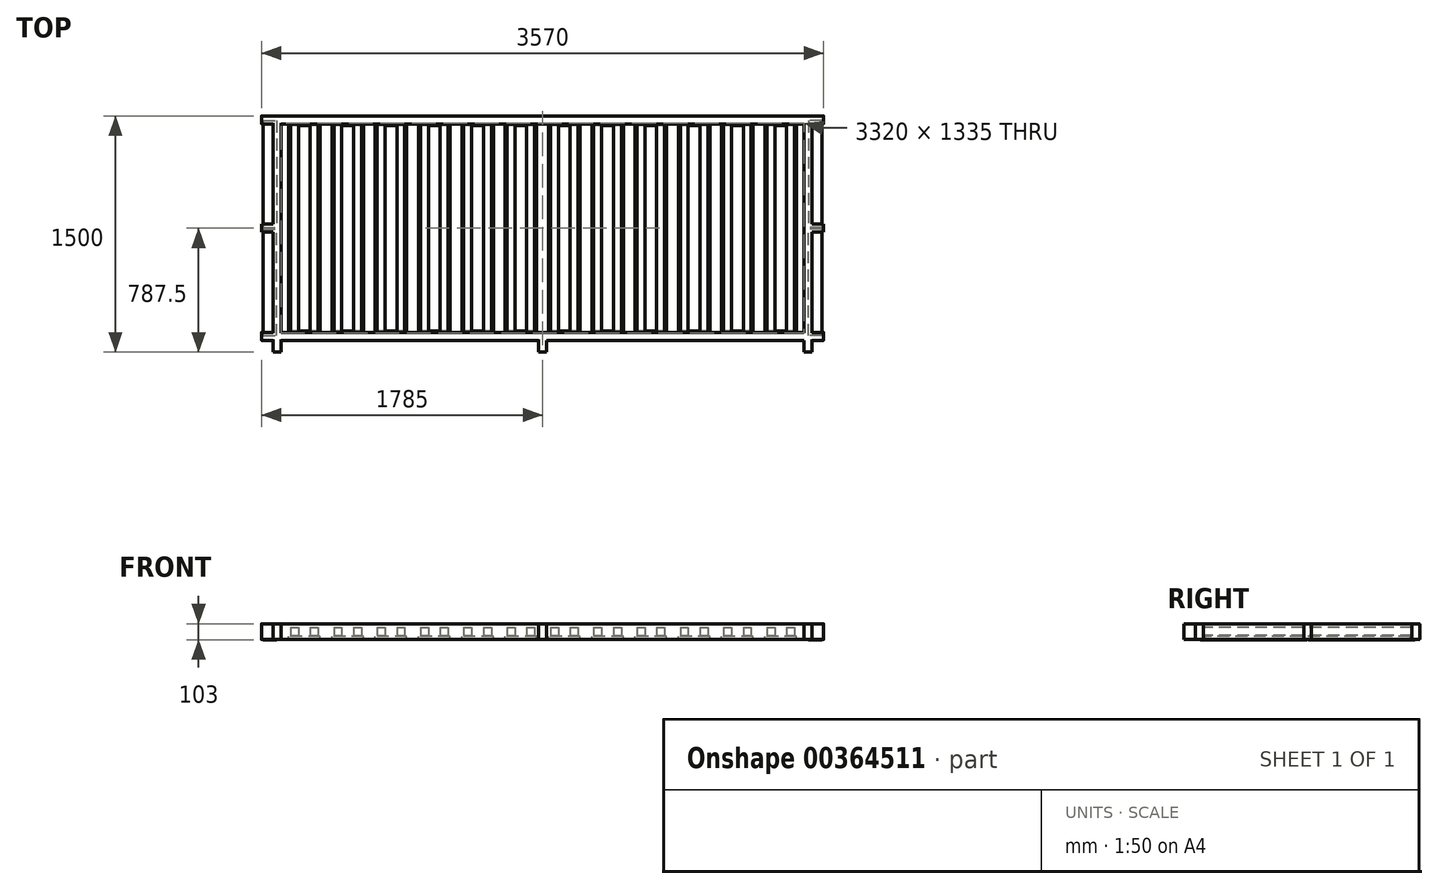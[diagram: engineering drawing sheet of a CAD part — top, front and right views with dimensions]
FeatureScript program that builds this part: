
annotation { "Feature Type Name" : "Feature", "Feature Type Description" : "" }
export const myFeature = defineFeature(function(context is Context, id is Id, definition is map)
    precondition{}
    {
        {
            var Q0;
            Q0=qCreatedBy(makeId("Top.planeOp"),FACE);
            var sketch = newSketch(context, id + "F0", { "sketchPlane" : qUnion([Q0])});
            skLineSegment(sketch, "E0.bottom", {"start": v(0, 0) * mm, "end": v(3570, 0) * mm, "construction": true});
            skLineSegment(sketch, "E0.top", {"start": v(0, 1500) * mm, "end": v(3570, 1500) * mm, "construction": true});
            skLineSegment(sketch, "E0.left", {"start": v(0, 0) * mm, "end": v(0, 1500) * mm, "construction": true});
            skLineSegment(sketch, "E0.right", {"start": v(3570, 0) * mm, "end": v(3570, 1500) * mm, "construction": true});
            skLineSegment(sketch, "E1.bottom", {"start": v(0, 1500) * mm, "end": v(3570, 1500) * mm});
            skLineSegment(sketch, "E1.top", {"start": v(0, 1450) * mm, "end": v(3570, 1450) * mm});
            skLineSegment(sketch, "E1.left", {"start": v(0, 1500) * mm, "end": v(0, 1450) * mm});
            skLineSegment(sketch, "E1.right", {"start": v(3570, 1500) * mm, "end": v(3570, 1450) * mm});
            skLineSegment(sketch, "E2.bottom", {"start": v(0, 125) * mm, "end": v(3570, 125) * mm});
            skLineSegment(sketch, "E2.top", {"start": v(0, 75) * mm, "end": v(3570, 75) * mm});
            skLineSegment(sketch, "E2.left", {"start": v(0, 125) * mm, "end": v(0, 75) * mm});
            skLineSegment(sketch, "E2.right", {"start": v(3570, 125) * mm, "end": v(3570, 75) * mm});
            skLineSegment(sketch, "E3.bottom", {"start": v(75, 1500) * mm, "end": v(125, 1500) * mm});
            skLineSegment(sketch, "E3.top", {"start": v(75, 0) * mm, "end": v(125, 0) * mm});
            skLineSegment(sketch, "E3.left", {"start": v(75, 1500) * mm, "end": v(75, 0) * mm});
            skLineSegment(sketch, "E3.right", {"start": v(125, 1500) * mm, "end": v(125, 0) * mm});
            skLineSegment(sketch, "E4.bottom", {"start": v(3445, 1500) * mm, "end": v(3495, 1500) * mm});
            skLineSegment(sketch, "E4.top", {"start": v(3445, 0) * mm, "end": v(3495, 0) * mm});
            skLineSegment(sketch, "E4.left", {"start": v(3445, 1500) * mm, "end": v(3445, 0) * mm});
            skLineSegment(sketch, "E4.right", {"start": v(3495, 1500) * mm, "end": v(3495, 0) * mm});
            skLineSegment(sketch, "E5.bottom", {"start": v(1810, 0) * mm, "end": v(1760, 0) * mm});
            skLineSegment(sketch, "E5.left", {"start": v(1810, 0) * mm, "end": v(1810, 75) * mm});
            skLineSegment(sketch, "E5.right", {"start": v(1760, 0) * mm, "end": v(1760, 75) * mm});
            skLineSegment(sketch, "E6", {"start": v(3495, 1450) * mm, "end": v(3495, 125) * mm, "construction": true});
            skLineSegment(sketch, "E7.bottom", {"start": v(3570, 812.5) * mm, "end": v(3495, 812.5) * mm});
            skLineSegment(sketch, "E7.top", {"start": v(3570, 762.5) * mm, "end": v(3495, 762.5) * mm});
            skLineSegment(sketch, "E7.left", {"start": v(3570, 812.5) * mm, "end": v(3570, 762.5) * mm});
            skLineSegment(sketch, "E8", {"start": v(75, 1450) * mm, "end": v(75, 125) * mm, "construction": true});
            skLineSegment(sketch, "E9.bottom", {"start": v(0, 812.5) * mm, "end": v(75, 812.5) * mm});
            skLineSegment(sketch, "E9.top", {"start": v(0, 762.5) * mm, "end": v(75, 762.5) * mm});
            skLineSegment(sketch, "E9.left", {"start": v(0, 812.5) * mm, "end": v(0, 762.5) * mm});
            skSolve(sketch);
        }
        {
            var Q0;
            Q0 = qSketchRegion(id + "F0", true);
            extrude(context, id + "F1", {"entities" : qUnion([Q0]), "depth" : 75 * mm, "hasSecondDirection" : true, "secondDirectionOppositeDirection" : true, "secondDirectionDepth" : 25 * mm});
        }
        {
            var Q0;
            {var subQ0=sQuery(id+"F0.wireOp",EDGE,"E1.top");Q0=makeQuery(id+"F1.opExtrude","CAP_EDGE",EDGE,{"disambiguationData":[OSD([subQ0]),TDD([makeQuery(id+"F0.imprint","IMPRINT",EDGE,{"disambiguationData":[TD([[makeQuery(id+"F0.imprint","INTERSECT",VERTEX,{"derivedFrom":[subQ0,sQuery(id+"F0.wireOp",EDGE,"E3.right")]}),-1.0]])],"derivedFrom":subQ0})])],"isStart":false});}
            var Q1;
            Q1=makeQuery(id+"F1.opExtrude","CAP_EDGE",EDGE,{"disambiguationData":[OSD([sQuery(id+"F0.wireOp",EDGE,"E1.bottom"),sQuery(id+"F0.wireOp",EDGE,"E3.bottom"),sQuery(id+"F0.wireOp",EDGE,"E4.bottom")])],"isStart":false});
            var Q2;
            {var subQ0=sQuery(id+"F0.wireOp",EDGE,"E2.bottom");Q2=makeQuery(id+"F1.opExtrude","CAP_EDGE",EDGE,{"disambiguationData":[OSD([subQ0]),TDD([makeQuery(id+"F0.imprint","IMPRINT",EDGE,{"disambiguationData":[TD([[makeQuery(id+"F0.imprint","INTERSECT",VERTEX,{"derivedFrom":[subQ0,sQuery(id+"F0.wireOp",EDGE,"E3.right")]}),-1.0]])],"derivedFrom":subQ0})])],"isStart":false});}
            var Q3;
            {var subQ0=sQuery(id+"F0.wireOp",EDGE,"E2.top");Q3=makeQuery(id+"F1.opExtrude","CAP_EDGE",EDGE,{"disambiguationData":[OSD([subQ0]),TDD([makeQuery(id+"F0.imprint","IMPRINT",EDGE,{"disambiguationData":[TD([[makeQuery(id+"F0.imprint","INTERSECT",VERTEX,{"derivedFrom":[subQ0,sQuery(id+"F0.wireOp",EDGE,"E3.right")]}),-1.0]])],"derivedFrom":subQ0})])],"isStart":false});}
            var Q4;
            {var subQ0=sQuery(id+"F0.wireOp",EDGE,"E2.top");Q4=makeQuery(id+"F1.opExtrude","CAP_EDGE",EDGE,{"disambiguationData":[OSD([subQ0]),TDD([makeQuery(id+"F0.imprint","IMPRINT",EDGE,{"disambiguationData":[TD([[makeQuery(id+"F0.imprint","INTERSECT",VERTEX,{"derivedFrom":[subQ0,sQuery(id+"F0.wireOp",EDGE,"E2.left")]}),-1.0]])],"derivedFrom":subQ0})])],"isStart":false});}
            var Q5;
            {var subQ0=sQuery(id+"F0.wireOp",EDGE,"E2.bottom");Q5=makeQuery(id+"F1.opExtrude","CAP_EDGE",EDGE,{"disambiguationData":[OSD([subQ0]),TDD([makeQuery(id+"F0.imprint","IMPRINT",EDGE,{"disambiguationData":[TD([[makeQuery(id+"F0.imprint","INTERSECT",VERTEX,{"derivedFrom":[subQ0,sQuery(id+"F0.wireOp",EDGE,"E2.left")]}),-1.0]])],"derivedFrom":subQ0})])],"isStart":false});}
            var Q6;
            {var subQ0=sQuery(id+"F0.wireOp",EDGE,"E2.bottom");Q6=makeQuery(id+"F1.opExtrude","CAP_EDGE",EDGE,{"disambiguationData":[OSD([subQ0]),TDD([makeQuery(id+"F0.imprint","IMPRINT",EDGE,{"disambiguationData":[TD([[makeQuery(id+"F0.imprint","INTERSECT",VERTEX,{"derivedFrom":[subQ0,sQuery(id+"F0.wireOp",EDGE,"E2.right")]}),1.0]])],"derivedFrom":subQ0})])],"isStart":false});}
            var Q7;
            {var subQ0=sQuery(id+"F0.wireOp",EDGE,"E2.top");Q7=makeQuery(id+"F1.opExtrude","CAP_EDGE",EDGE,{"disambiguationData":[OSD([subQ0]),TDD([makeQuery(id+"F0.imprint","IMPRINT",EDGE,{"disambiguationData":[TD([[makeQuery(id+"F0.imprint","INTERSECT",VERTEX,{"derivedFrom":[subQ0,sQuery(id+"F0.wireOp",EDGE,"E2.right")]}),1.0]])],"derivedFrom":subQ0})])],"isStart":false});}
            var Q8;
            {var subQ0=sQuery(id+"F0.wireOp",EDGE,"E1.top");Q8=makeQuery(id+"F1.opExtrude","CAP_EDGE",EDGE,{"disambiguationData":[OSD([subQ0]),TDD([makeQuery(id+"F0.imprint","IMPRINT",EDGE,{"disambiguationData":[TD([[makeQuery(id+"F0.imprint","INTERSECT",VERTEX,{"derivedFrom":[subQ0,sQuery(id+"F0.wireOp",EDGE,"E1.right")]}),1.0]])],"derivedFrom":subQ0})])],"isStart":false});}
            var Q9;
            {var subQ0=sQuery(id+"F0.wireOp",EDGE,"E1.top");Q9=makeQuery(id+"F1.opExtrude","CAP_EDGE",EDGE,{"disambiguationData":[OSD([subQ0]),TDD([makeQuery(id+"F0.imprint","IMPRINT",EDGE,{"disambiguationData":[TD([[makeQuery(id+"F0.imprint","INTERSECT",VERTEX,{"derivedFrom":[subQ0,sQuery(id+"F0.wireOp",EDGE,"E1.left")]}),-1.0]])],"derivedFrom":subQ0})])],"isStart":false});}
            var Q10;
            Q10=makeQuery(id+"F1.opExtrude","CAP_EDGE",EDGE,{"disambiguationData":[OSD([sQuery(id+"F0.wireOp",EDGE,"E1.bottom"),sQuery(id+"F0.wireOp",EDGE,"E3.bottom"),sQuery(id+"F0.wireOp",EDGE,"E4.bottom")])],"isStart":true});
            var Q11;
            {var subQ0=sQuery(id+"F0.wireOp",EDGE,"E1.top");Q11=makeQuery(id+"F1.opExtrude","CAP_EDGE",EDGE,{"disambiguationData":[OSD([subQ0]),TDD([makeQuery(id+"F0.imprint","IMPRINT",EDGE,{"disambiguationData":[TD([[makeQuery(id+"F0.imprint","INTERSECT",VERTEX,{"derivedFrom":[subQ0,sQuery(id+"F0.wireOp",EDGE,"E3.right")]}),-1.0]])],"derivedFrom":subQ0})])],"isStart":true});}
            var Q12;
            {var subQ0=sQuery(id+"F0.wireOp",EDGE,"E1.top");Q12=makeQuery(id+"F1.opExtrude","CAP_EDGE",EDGE,{"disambiguationData":[OSD([subQ0]),TDD([makeQuery(id+"F0.imprint","IMPRINT",EDGE,{"disambiguationData":[TD([[makeQuery(id+"F0.imprint","INTERSECT",VERTEX,{"derivedFrom":[subQ0,sQuery(id+"F0.wireOp",EDGE,"E1.right")]}),1.0]])],"derivedFrom":subQ0})])],"isStart":true});}
            var Q13;
            {var subQ0=sQuery(id+"F0.wireOp",EDGE,"E2.top");Q13=makeQuery(id+"F1.opExtrude","CAP_EDGE",EDGE,{"disambiguationData":[OSD([subQ0]),TDD([makeQuery(id+"F0.imprint","IMPRINT",EDGE,{"disambiguationData":[TD([[makeQuery(id+"F0.imprint","INTERSECT",VERTEX,{"derivedFrom":[subQ0,sQuery(id+"F0.wireOp",EDGE,"E2.right")]}),1.0]])],"derivedFrom":subQ0})])],"isStart":true});}
            var Q14;
            {var subQ0=sQuery(id+"F0.wireOp",EDGE,"E2.bottom");Q14=makeQuery(id+"F1.opExtrude","CAP_EDGE",EDGE,{"disambiguationData":[OSD([subQ0]),TDD([makeQuery(id+"F0.imprint","IMPRINT",EDGE,{"disambiguationData":[TD([[makeQuery(id+"F0.imprint","INTERSECT",VERTEX,{"derivedFrom":[subQ0,sQuery(id+"F0.wireOp",EDGE,"E2.right")]}),1.0]])],"derivedFrom":subQ0})])],"isStart":true});}
            var Q15;
            {var subQ0=sQuery(id+"F0.wireOp",EDGE,"E2.bottom");Q15=makeQuery(id+"F1.opExtrude","CAP_EDGE",EDGE,{"disambiguationData":[OSD([subQ0]),TDD([makeQuery(id+"F0.imprint","IMPRINT",EDGE,{"disambiguationData":[TD([[makeQuery(id+"F0.imprint","INTERSECT",VERTEX,{"derivedFrom":[subQ0,sQuery(id+"F0.wireOp",EDGE,"E3.right")]}),-1.0]])],"derivedFrom":subQ0})])],"isStart":true});}
            var Q16;
            {var subQ0=sQuery(id+"F0.wireOp",EDGE,"E2.top");Q16=makeQuery(id+"F1.opExtrude","CAP_EDGE",EDGE,{"disambiguationData":[OSD([subQ0]),TDD([makeQuery(id+"F0.imprint","IMPRINT",EDGE,{"disambiguationData":[TD([[makeQuery(id+"F0.imprint","INTERSECT",VERTEX,{"derivedFrom":[subQ0,sQuery(id+"F0.wireOp",EDGE,"E3.right")]}),-1.0]])],"derivedFrom":subQ0})])],"isStart":true});}
            var Q17;
            {var subQ0=sQuery(id+"F0.wireOp",EDGE,"E2.bottom");Q17=makeQuery(id+"F1.opExtrude","CAP_EDGE",EDGE,{"disambiguationData":[OSD([subQ0]),TDD([makeQuery(id+"F0.imprint","IMPRINT",EDGE,{"disambiguationData":[TD([[makeQuery(id+"F0.imprint","INTERSECT",VERTEX,{"derivedFrom":[subQ0,sQuery(id+"F0.wireOp",EDGE,"E2.left")]}),-1.0]])],"derivedFrom":subQ0})])],"isStart":true});}
            var Q18;
            {var subQ0=sQuery(id+"F0.wireOp",EDGE,"E2.top");Q18=makeQuery(id+"F1.opExtrude","CAP_EDGE",EDGE,{"disambiguationData":[OSD([subQ0]),TDD([makeQuery(id+"F0.imprint","IMPRINT",EDGE,{"disambiguationData":[TD([[makeQuery(id+"F0.imprint","INTERSECT",VERTEX,{"derivedFrom":[subQ0,sQuery(id+"F0.wireOp",EDGE,"E2.left")]}),-1.0]])],"derivedFrom":subQ0})])],"isStart":true});}
            var Q19;
            {var subQ0=sQuery(id+"F0.wireOp",EDGE,"E1.top");Q19=makeQuery(id+"F1.opExtrude","CAP_EDGE",EDGE,{"disambiguationData":[OSD([subQ0]),TDD([makeQuery(id+"F0.imprint","IMPRINT",EDGE,{"disambiguationData":[TD([[makeQuery(id+"F0.imprint","INTERSECT",VERTEX,{"derivedFrom":[subQ0,sQuery(id+"F0.wireOp",EDGE,"E1.left")]}),-1.0]])],"derivedFrom":subQ0})])],"isStart":true});}
            fillet(context, id + "F2", {"entities" : qUnion([Q0, Q1, Q2, Q3, Q4, Q5, Q6, Q7, Q8, Q9, Q10, Q11, Q12, Q13, Q14, Q15, Q16, Q17, Q18, Q19]), "radius" : 5 * mm, "tangentPropagation" : true, "allowEdgeOverflow" : false});
        }
        {
            var Q0;
            Q0=qCreatedBy(makeId("Top.planeOp"),FACE);
            var sketch = newSketch(context, id + "F3", { "sketchPlane" : qUnion([Q0])});
            skLineSegment(sketch, "E10.bottom", {"start": v(185, 1450) * mm, "end": v(235, 1450) * mm});
            skLineSegment(sketch, "E10.top", {"start": v(185, 125) * mm, "end": v(235, 125) * mm});
            skLineSegment(sketch, "E10.left", {"start": v(185, 1450) * mm, "end": v(185, 125) * mm});
            skLineSegment(sketch, "E10.right", {"start": v(235, 1450) * mm, "end": v(235, 125) * mm});
            skLineSegment(sketch, "E11.bottom", {"start": v(310, 1450) * mm, "end": v(360, 1450) * mm});
            skLineSegment(sketch, "E11.top", {"start": v(310, 125) * mm, "end": v(360, 125) * mm});
            skLineSegment(sketch, "E11.left", {"start": v(310, 1450) * mm, "end": v(310, 125) * mm});
            skLineSegment(sketch, "E11.right", {"start": v(360, 1450) * mm, "end": v(360, 125) * mm});
            skLineSegment(sketch, "E12", {"start": v(235, 125) * mm, "end": v(387, 125) * mm, "construction": true});
            skLineSegment(sketch, "E13", {"start": v(235, 1450) * mm, "end": v(386.34, 1450) * mm, "construction": true});
            skLineSegment(sketch, "E14.1.0.0", {"start": v(635, 1450) * mm, "end": v(635, 125) * mm});
            skLineSegment(sketch, "E14.1.0.1", {"start": v(585, 1450) * mm, "end": v(585, 125) * mm});
            skLineSegment(sketch, "E14.1.0.2", {"start": v(510, 1450) * mm, "end": v(510, 125) * mm});
            skLineSegment(sketch, "E14.1.0.3", {"start": v(460, 1450) * mm, "end": v(460, 125) * mm});
            skLineSegment(sketch, "E14.1.0.4", {"start": v(460, 125) * mm, "end": v(510, 125) * mm});
            skLineSegment(sketch, "E14.1.0.5", {"start": v(460, 1450) * mm, "end": v(510, 1450) * mm});
            skLineSegment(sketch, "E14.1.0.6", {"start": v(585, 125) * mm, "end": v(635, 125) * mm});
            skLineSegment(sketch, "E14.1.0.7", {"start": v(585, 1450) * mm, "end": v(635, 1450) * mm});
            skLineSegment(sketch, "E14.2.0.0", {"start": v(910, 1450) * mm, "end": v(910, 125) * mm});
            skLineSegment(sketch, "E14.2.0.1", {"start": v(860, 1450) * mm, "end": v(860, 125) * mm});
            skLineSegment(sketch, "E14.2.0.2", {"start": v(785, 1450) * mm, "end": v(785, 125) * mm});
            skLineSegment(sketch, "E14.2.0.3", {"start": v(735, 1450) * mm, "end": v(735, 125) * mm});
            skLineSegment(sketch, "E14.2.0.4", {"start": v(735, 125) * mm, "end": v(785, 125) * mm});
            skLineSegment(sketch, "E14.2.0.5", {"start": v(735, 1450) * mm, "end": v(785, 1450) * mm});
            skLineSegment(sketch, "E14.2.0.6", {"start": v(860, 125) * mm, "end": v(910, 125) * mm});
            skLineSegment(sketch, "E14.2.0.7", {"start": v(860, 1450) * mm, "end": v(910, 1450) * mm});
            skLineSegment(sketch, "E14.3.0.0", {"start": v(1185, 1450) * mm, "end": v(1185, 125) * mm});
            skLineSegment(sketch, "E14.3.0.1", {"start": v(1135, 1450) * mm, "end": v(1135, 125) * mm});
            skLineSegment(sketch, "E14.3.0.2", {"start": v(1060, 1450) * mm, "end": v(1060, 125) * mm});
            skLineSegment(sketch, "E14.3.0.3", {"start": v(1010, 1450) * mm, "end": v(1010, 125) * mm});
            skLineSegment(sketch, "E14.3.0.4", {"start": v(1010, 125) * mm, "end": v(1060, 125) * mm});
            skLineSegment(sketch, "E14.3.0.5", {"start": v(1010, 1450) * mm, "end": v(1060, 1450) * mm});
            skLineSegment(sketch, "E14.3.0.6", {"start": v(1135, 125) * mm, "end": v(1185, 125) * mm});
            skLineSegment(sketch, "E14.3.0.7", {"start": v(1135, 1450) * mm, "end": v(1185, 1450) * mm});
            skLineSegment(sketch, "E14.4.0.0", {"start": v(1460, 1450) * mm, "end": v(1460, 125) * mm});
            skLineSegment(sketch, "E14.4.0.1", {"start": v(1410, 1450) * mm, "end": v(1410, 125) * mm});
            skLineSegment(sketch, "E14.4.0.2", {"start": v(1335, 1450) * mm, "end": v(1335, 125) * mm});
            skLineSegment(sketch, "E14.4.0.3", {"start": v(1285, 1450) * mm, "end": v(1285, 125) * mm});
            skLineSegment(sketch, "E14.4.0.4", {"start": v(1285, 125) * mm, "end": v(1335, 125) * mm});
            skLineSegment(sketch, "E14.4.0.5", {"start": v(1285, 1450) * mm, "end": v(1335, 1450) * mm});
            skLineSegment(sketch, "E14.4.0.6", {"start": v(1410, 125) * mm, "end": v(1460, 125) * mm});
            skLineSegment(sketch, "E14.4.0.7", {"start": v(1410, 1450) * mm, "end": v(1460, 1450) * mm});
            skLineSegment(sketch, "E14.5.0.0", {"start": v(1735, 1450) * mm, "end": v(1735, 125) * mm});
            skLineSegment(sketch, "E14.5.0.1", {"start": v(1685, 1450) * mm, "end": v(1685, 125) * mm});
            skLineSegment(sketch, "E14.5.0.2", {"start": v(1610, 1450) * mm, "end": v(1610, 125) * mm});
            skLineSegment(sketch, "E14.5.0.3", {"start": v(1560, 1450) * mm, "end": v(1560, 125) * mm});
            skLineSegment(sketch, "E14.5.0.4", {"start": v(1560, 125) * mm, "end": v(1610, 125) * mm});
            skLineSegment(sketch, "E14.5.0.5", {"start": v(1560, 1450) * mm, "end": v(1610, 1450) * mm});
            skLineSegment(sketch, "E14.5.0.6", {"start": v(1685, 125) * mm, "end": v(1735, 125) * mm});
            skLineSegment(sketch, "E14.5.0.7", {"start": v(1685, 1450) * mm, "end": v(1735, 1450) * mm});
            skLineSegment(sketch, "E14.6.0.0", {"start": v(2010, 1450) * mm, "end": v(2010, 125) * mm});
            skLineSegment(sketch, "E14.6.0.1", {"start": v(1960, 1450) * mm, "end": v(1960, 125) * mm});
            skLineSegment(sketch, "E14.6.0.2", {"start": v(1885, 1450) * mm, "end": v(1885, 125) * mm});
            skLineSegment(sketch, "E14.6.0.3", {"start": v(1835, 1450) * mm, "end": v(1835, 125) * mm});
            skLineSegment(sketch, "E14.6.0.4", {"start": v(1835, 125) * mm, "end": v(1885, 125) * mm});
            skLineSegment(sketch, "E14.6.0.5", {"start": v(1835, 1450) * mm, "end": v(1885, 1450) * mm});
            skLineSegment(sketch, "E14.6.0.6", {"start": v(1960, 125) * mm, "end": v(2010, 125) * mm});
            skLineSegment(sketch, "E14.6.0.7", {"start": v(1960, 1450) * mm, "end": v(2010, 1450) * mm});
            skLineSegment(sketch, "E14.7.0.0", {"start": v(2285, 1450) * mm, "end": v(2285, 125) * mm});
            skLineSegment(sketch, "E14.7.0.1", {"start": v(2235, 1450) * mm, "end": v(2235, 125) * mm});
            skLineSegment(sketch, "E14.7.0.2", {"start": v(2160, 1450) * mm, "end": v(2160, 125) * mm});
            skLineSegment(sketch, "E14.7.0.3", {"start": v(2110, 1450) * mm, "end": v(2110, 125) * mm});
            skLineSegment(sketch, "E14.7.0.4", {"start": v(2110, 125) * mm, "end": v(2160, 125) * mm});
            skLineSegment(sketch, "E14.7.0.5", {"start": v(2110, 1450) * mm, "end": v(2160, 1450) * mm});
            skLineSegment(sketch, "E14.7.0.6", {"start": v(2235, 125) * mm, "end": v(2285, 125) * mm});
            skLineSegment(sketch, "E14.7.0.7", {"start": v(2235, 1450) * mm, "end": v(2285, 1450) * mm});
            skLineSegment(sketch, "E14.8.0.0", {"start": v(2560, 1450) * mm, "end": v(2560, 125) * mm});
            skLineSegment(sketch, "E14.8.0.1", {"start": v(2510, 1450) * mm, "end": v(2510, 125) * mm});
            skLineSegment(sketch, "E14.8.0.2", {"start": v(2435, 1450) * mm, "end": v(2435, 125) * mm});
            skLineSegment(sketch, "E14.8.0.3", {"start": v(2385, 1450) * mm, "end": v(2385, 125) * mm});
            skLineSegment(sketch, "E14.8.0.4", {"start": v(2385, 125) * mm, "end": v(2435, 125) * mm});
            skLineSegment(sketch, "E14.8.0.5", {"start": v(2385, 1450) * mm, "end": v(2435, 1450) * mm});
            skLineSegment(sketch, "E14.8.0.6", {"start": v(2510, 125) * mm, "end": v(2560, 125) * mm});
            skLineSegment(sketch, "E14.8.0.7", {"start": v(2510, 1450) * mm, "end": v(2560, 1450) * mm});
            skLineSegment(sketch, "E14.9.0.0", {"start": v(2835, 1450) * mm, "end": v(2835, 125) * mm});
            skLineSegment(sketch, "E14.9.0.1", {"start": v(2785, 1450) * mm, "end": v(2785, 125) * mm});
            skLineSegment(sketch, "E14.9.0.2", {"start": v(2710, 1450) * mm, "end": v(2710, 125) * mm});
            skLineSegment(sketch, "E14.9.0.3", {"start": v(2660, 1450) * mm, "end": v(2660, 125) * mm});
            skLineSegment(sketch, "E14.9.0.4", {"start": v(2660, 125) * mm, "end": v(2710, 125) * mm});
            skLineSegment(sketch, "E14.9.0.5", {"start": v(2660, 1450) * mm, "end": v(2710, 1450) * mm});
            skLineSegment(sketch, "E14.9.0.6", {"start": v(2785, 125) * mm, "end": v(2835, 125) * mm});
            skLineSegment(sketch, "E14.9.0.7", {"start": v(2785, 1450) * mm, "end": v(2835, 1450) * mm});
            skLineSegment(sketch, "E14.10.0.0", {"start": v(3110, 1450) * mm, "end": v(3110, 125) * mm});
            skLineSegment(sketch, "E14.10.0.1", {"start": v(3060, 1450) * mm, "end": v(3060, 125) * mm});
            skLineSegment(sketch, "E14.10.0.2", {"start": v(2985, 1450) * mm, "end": v(2985, 125) * mm});
            skLineSegment(sketch, "E14.10.0.3", {"start": v(2935, 1450) * mm, "end": v(2935, 125) * mm});
            skLineSegment(sketch, "E14.10.0.4", {"start": v(2935, 125) * mm, "end": v(2985, 125) * mm});
            skLineSegment(sketch, "E14.10.0.5", {"start": v(2935, 1450) * mm, "end": v(2985, 1450) * mm});
            skLineSegment(sketch, "E14.10.0.6", {"start": v(3060, 125) * mm, "end": v(3110, 125) * mm});
            skLineSegment(sketch, "E14.10.0.7", {"start": v(3060, 1450) * mm, "end": v(3110, 1450) * mm});
            skLineSegment(sketch, "E14.11.0.0", {"start": v(3385, 1450) * mm, "end": v(3385, 125) * mm});
            skLineSegment(sketch, "E14.11.0.1", {"start": v(3335, 1450) * mm, "end": v(3335, 125) * mm});
            skLineSegment(sketch, "E14.11.0.2", {"start": v(3260, 1450) * mm, "end": v(3260, 125) * mm});
            skLineSegment(sketch, "E14.11.0.3", {"start": v(3210, 1450) * mm, "end": v(3210, 125) * mm});
            skLineSegment(sketch, "E14.11.0.4", {"start": v(3210, 125) * mm, "end": v(3260, 125) * mm});
            skLineSegment(sketch, "E14.11.0.5", {"start": v(3210, 1450) * mm, "end": v(3260, 1450) * mm});
            skLineSegment(sketch, "E14.11.0.6", {"start": v(3335, 125) * mm, "end": v(3385, 125) * mm});
            skLineSegment(sketch, "E14.11.0.7", {"start": v(3335, 1450) * mm, "end": v(3385, 1450) * mm});
            skLineSegment(sketch, "E14.direction1", {"start": v(185, 125) * mm, "end": v(460, 125) * mm, "construction": true});
            skSolve(sketch);
        }
        {
            var Q0;
            Q0 = qSketchRegion(id + "F3", true);
            extrude(context, id + "F4", {"entities" : qUnion([Q0]), "depth" : 50 * mm});
        }
        {
            var Q0;
            Q0=makeQuery(id+"F4.opExtrude","CAP_FACE",FACE,{"disambiguationData":[OSD([sQuery(id+"F3.wireOp",EDGE,"E14.11.0.0"),sQuery(id+"F3.wireOp",EDGE,"E14.11.0.1"),sQuery(id+"F3.wireOp",EDGE,"E14.11.0.6"),sQuery(id+"F3.wireOp",EDGE,"E14.11.0.7")])],"isStart":true});
            var sketch = newSketch(context, id + "F5", { "sketchPlane" : qUnion([Q0])});
            skLineSegment(sketch, "E15.bottom", {"start": v(3397.7, -1440) * mm, "end": v(3197.7, -1440) * mm});
            skLineSegment(sketch, "E15.top", {"start": v(3397.7, -135) * mm, "end": v(3197.7, -135) * mm});
            skLineSegment(sketch, "E15.left", {"start": v(3397.7, -1440) * mm, "end": v(3397.7, -135) * mm});
            skLineSegment(sketch, "E15.right", {"start": v(3197.7, -1440) * mm, "end": v(3197.7, -135) * mm});
            skLineSegment(sketch, "E16.1.0.0", {"start": v(2922.7, -1440) * mm, "end": v(2922.7, -135) * mm});
            skLineSegment(sketch, "E16.1.0.1", {"start": v(3122.7, -1440) * mm, "end": v(2922.7, -1440) * mm});
            skLineSegment(sketch, "E16.1.0.2", {"start": v(3122.7, -135) * mm, "end": v(2922.7, -135) * mm});
            skLineSegment(sketch, "E16.1.0.3", {"start": v(3122.7, -1440) * mm, "end": v(3122.7, -135) * mm});
            skLineSegment(sketch, "E16.2.0.0", {"start": v(2647.7, -1440) * mm, "end": v(2647.7, -135) * mm});
            skLineSegment(sketch, "E16.2.0.1", {"start": v(2847.7, -1440) * mm, "end": v(2647.7, -1440) * mm});
            skLineSegment(sketch, "E16.2.0.2", {"start": v(2847.7, -135) * mm, "end": v(2647.7, -135) * mm});
            skLineSegment(sketch, "E16.2.0.3", {"start": v(2847.7, -1440) * mm, "end": v(2847.7, -135) * mm});
            skLineSegment(sketch, "E16.3.0.0", {"start": v(2372.7, -1440) * mm, "end": v(2372.7, -135) * mm});
            skLineSegment(sketch, "E16.3.0.1", {"start": v(2572.7, -1440) * mm, "end": v(2372.7, -1440) * mm});
            skLineSegment(sketch, "E16.3.0.2", {"start": v(2572.7, -135) * mm, "end": v(2372.7, -135) * mm});
            skLineSegment(sketch, "E16.3.0.3", {"start": v(2572.7, -1440) * mm, "end": v(2572.7, -135) * mm});
            skLineSegment(sketch, "E16.4.0.0", {"start": v(2097.7, -1440) * mm, "end": v(2097.7, -135) * mm});
            skLineSegment(sketch, "E16.4.0.1", {"start": v(2297.7, -1440) * mm, "end": v(2097.7, -1440) * mm});
            skLineSegment(sketch, "E16.4.0.2", {"start": v(2297.7, -135) * mm, "end": v(2097.7, -135) * mm});
            skLineSegment(sketch, "E16.4.0.3", {"start": v(2297.7, -1440) * mm, "end": v(2297.7, -135) * mm});
            skLineSegment(sketch, "E16.5.0.0", {"start": v(1822.7, -1440) * mm, "end": v(1822.7, -135) * mm});
            skLineSegment(sketch, "E16.5.0.1", {"start": v(2022.7, -1440) * mm, "end": v(1822.7, -1440) * mm});
            skLineSegment(sketch, "E16.5.0.2", {"start": v(2022.7, -135) * mm, "end": v(1822.7, -135) * mm});
            skLineSegment(sketch, "E16.5.0.3", {"start": v(2022.7, -1440) * mm, "end": v(2022.7, -135) * mm});
            skLineSegment(sketch, "E16.6.0.0", {"start": v(1547.7, -1440) * mm, "end": v(1547.7, -135) * mm});
            skLineSegment(sketch, "E16.6.0.1", {"start": v(1747.7, -1440) * mm, "end": v(1547.7, -1440) * mm});
            skLineSegment(sketch, "E16.6.0.2", {"start": v(1747.7, -135) * mm, "end": v(1547.7, -135) * mm});
            skLineSegment(sketch, "E16.6.0.3", {"start": v(1747.7, -1440) * mm, "end": v(1747.7, -135) * mm});
            skLineSegment(sketch, "E16.7.0.0", {"start": v(1272.7, -1440) * mm, "end": v(1272.7, -135) * mm});
            skLineSegment(sketch, "E16.7.0.1", {"start": v(1472.7, -1440) * mm, "end": v(1272.7, -1440) * mm});
            skLineSegment(sketch, "E16.7.0.2", {"start": v(1472.7, -135) * mm, "end": v(1272.7, -135) * mm});
            skLineSegment(sketch, "E16.7.0.3", {"start": v(1472.7, -1440) * mm, "end": v(1472.7, -135) * mm});
            skLineSegment(sketch, "E16.8.0.0", {"start": v(997.7, -1440) * mm, "end": v(997.7, -135) * mm});
            skLineSegment(sketch, "E16.8.0.1", {"start": v(1197.7, -1440) * mm, "end": v(997.7, -1440) * mm});
            skLineSegment(sketch, "E16.8.0.2", {"start": v(1197.7, -135) * mm, "end": v(997.7, -135) * mm});
            skLineSegment(sketch, "E16.8.0.3", {"start": v(1197.7, -1440) * mm, "end": v(1197.7, -135) * mm});
            skLineSegment(sketch, "E16.9.0.0", {"start": v(722.7, -1440) * mm, "end": v(722.7, -135) * mm});
            skLineSegment(sketch, "E16.9.0.1", {"start": v(922.7, -1440) * mm, "end": v(722.7, -1440) * mm});
            skLineSegment(sketch, "E16.9.0.2", {"start": v(922.7, -135) * mm, "end": v(722.7, -135) * mm});
            skLineSegment(sketch, "E16.9.0.3", {"start": v(922.7, -1440) * mm, "end": v(922.7, -135) * mm});
            skLineSegment(sketch, "E16.10.0.0", {"start": v(447.7, -1440) * mm, "end": v(447.7, -135) * mm});
            skLineSegment(sketch, "E16.10.0.1", {"start": v(647.7, -1440) * mm, "end": v(447.7, -1440) * mm});
            skLineSegment(sketch, "E16.10.0.2", {"start": v(647.7, -135) * mm, "end": v(447.7, -135) * mm});
            skLineSegment(sketch, "E16.10.0.3", {"start": v(647.7, -1440) * mm, "end": v(647.7, -135) * mm});
            skLineSegment(sketch, "E16.11.0.0", {"start": v(172.7, -1440) * mm, "end": v(172.7, -135) * mm});
            skLineSegment(sketch, "E16.11.0.1", {"start": v(372.7, -1440) * mm, "end": v(172.7, -1440) * mm});
            skLineSegment(sketch, "E16.11.0.2", {"start": v(372.7, -135) * mm, "end": v(172.7, -135) * mm});
            skLineSegment(sketch, "E16.11.0.3", {"start": v(372.7, -1440) * mm, "end": v(372.7, -135) * mm});
            skLineSegment(sketch, "E16.direction1", {"start": v(3197.7, -1440) * mm, "end": v(2922.7, -1440) * mm, "construction": true});
            skSolve(sketch);
        }
        {
            var Q0;
            Q0 = qSketchRegion(id + "F5", true);
            extrude(context, id + "F6", {"entities" : qUnion([Q0]), "depth" : 25 * mm, "hasSecondDirection" : true, "secondDirectionOppositeDirection" : false, "secondDirectionDepth" : 6 * mm});
        }
        {
            var Q0;
            Q0=makeQuery(id+"F1.opExtrude","CAP_FACE",FACE,{"disambiguationData":[OSD([sQuery(id+"F0.wireOp",EDGE,"E1.bottom"),sQuery(id+"F0.wireOp",EDGE,"E1.top"),sQuery(id+"F0.wireOp",EDGE,"E1.left"),sQuery(id+"F0.wireOp",EDGE,"E1.right"),sQuery(id+"F0.wireOp",EDGE,"E2.bottom"),sQuery(id+"F0.wireOp",EDGE,"E2.top"),sQuery(id+"F0.wireOp",EDGE,"E2.left"),sQuery(id+"F0.wireOp",EDGE,"E2.right"),sQuery(id+"F0.wireOp",EDGE,"E3.bottom"),sQuery(id+"F0.wireOp",EDGE,"E3.top"),sQuery(id+"F0.wireOp",EDGE,"E3.left"),sQuery(id+"F0.wireOp",EDGE,"E3.right"),sQuery(id+"F0.wireOp",EDGE,"E4.bottom"),sQuery(id+"F0.wireOp",EDGE,"E4.top"),sQuery(id+"F0.wireOp",EDGE,"E4.left"),sQuery(id+"F0.wireOp",EDGE,"E4.right"),sQuery(id+"F0.wireOp",EDGE,"E5.bottom"),sQuery(id+"F0.wireOp",EDGE,"E5.left"),sQuery(id+"F0.wireOp",EDGE,"E5.right"),sQuery(id+"F0.wireOp",EDGE,"E7.bottom"),sQuery(id+"F0.wireOp",EDGE,"E7.top"),sQuery(id+"F0.wireOp",EDGE,"E7.left"),sQuery(id+"F0.wireOp",EDGE,"E9.bottom"),sQuery(id+"F0.wireOp",EDGE,"E9.top"),sQuery(id+"F0.wireOp",EDGE,"E9.left")])],"isStart":true});
            var sketch = newSketch(context, id + "F7", { "sketchPlane" : qUnion([Q0])});
            skLineSegment(sketch, "E17.bottom", {"start": v(3560, -1470) * mm, "end": v(3475, -1470) * mm});
            skLineSegment(sketch, "E17.top", {"start": v(3560, -792.5) * mm, "end": v(3475, -792.5) * mm});
            skLineSegment(sketch, "E17.left", {"start": v(3560, -1470) * mm, "end": v(3560, -792.5) * mm});
            skLineSegment(sketch, "E17.right", {"start": v(3475, -1470) * mm, "end": v(3475, -792.5) * mm});
            skLineSegment(sketch, "E18", {"start": v(3445, -787.5) * mm, "end": v(3710.6, -787.5) * mm, "construction": true});
            skLineSegment(sketch, "E19.MirrorCS", {"start": v(3560, -105) * mm, "end": v(3475, -105) * mm});
            skLineSegment(sketch, "E20.MirrorCS", {"start": v(3475, -105) * mm, "end": v(3475, -782.5) * mm});
            skLineSegment(sketch, "E21.MirrorCS", {"start": v(3560, -105) * mm, "end": v(3560, -782.5) * mm});
            skLineSegment(sketch, "E22.MirrorCS", {"start": v(3560, -782.5) * mm, "end": v(3475, -782.5) * mm});
            skLineSegment(sketch, "E23", {"start": v(1785, 0) * mm, "end": v(1785, -316.49) * mm, "construction": true});
            skPoint(sketch, "E23.endSnap0", {"position": v(1785, 0) * mm});
            skLineSegment(sketch, "E24.MirrorCS", {"start": v(10, -1470) * mm, "end": v(95, -1470) * mm});
            skLineSegment(sketch, "E25.MirrorCS", {"start": v(10, -105) * mm, "end": v(95, -105) * mm});
            skLineSegment(sketch, "E26.MirrorCS", {"start": v(10, -1470) * mm, "end": v(10, -792.5) * mm});
            skLineSegment(sketch, "E27.MirrorCS", {"start": v(95, -105) * mm, "end": v(95, -782.5) * mm});
            skLineSegment(sketch, "E28.MirrorCS", {"start": v(95, -1470) * mm, "end": v(95, -792.5) * mm});
            skLineSegment(sketch, "E29.MirrorCS", {"start": v(10, -792.5) * mm, "end": v(95, -792.5) * mm});
            skLineSegment(sketch, "E30.MirrorCS", {"start": v(10, -782.5) * mm, "end": v(95, -782.5) * mm});
            skLineSegment(sketch, "E31.MirrorCS", {"start": v(10, -105) * mm, "end": v(10, -782.5) * mm});
            skSolve(sketch);
        }
        {
            var Q0;
            Q0 = qSketchRegion(id + "F7", true);
            extrude(context, id + "F8", {"entities" : qUnion([Q0]), "operationType" : NewBodyOperationType.ADD, "depth" : 3 * mm});
        }
    });
